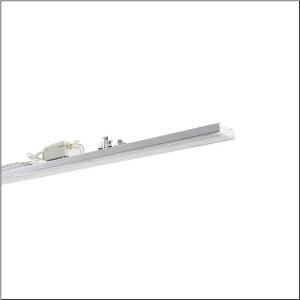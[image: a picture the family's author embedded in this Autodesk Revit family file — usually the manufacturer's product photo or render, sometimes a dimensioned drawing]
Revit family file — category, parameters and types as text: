
# Revit family: licross_r__21_recessed_ho_52tl12dn1e5m_37b9
name_source: partatom
category: Lighting Fixtures
units: mm (PartAtom-declared; Revit-internal decimal feet)

## family parameters
Cut with Voids When Loaded = No
Host = Face
Light Source = No
Part Type = Normal
Room Calculation Point = No
Round Connector Dimension = Use Diameter
Shared = No

## types (1)
- --- (1 x LED, 14510 lm, 84.6 W, 3500K)
    Apparent Load = 85 VA
    CIE Flux Codes = 69 91 98 100 100
    Color Rendering = 80
    Color Temperature = 3500K
    Default Elevation = 1800 mm
    Description = Licross® 21 Recessed HO, luminaire insert, of sheet steel, galvanised, coil coated, white, length: 1.500mm, width: 66mm, height: 67mm, LED rated luminous flux: 14.510lm, light colour: 835, control gear: DALI 2, with plug, 5-pole, with phase selection, mains connection: 220..240V, AC, 50/60Hz, rated input power: 85W, halogen-free wiring, primary optical cover: cover, of PMMA, light emission: direct distribution, primary light characteristic: symmetric, protection rating (complete): IP40, insulation class (complete): insulation class I (protective earthing), certification: CE, ENEC, VDE, UKCA, protection symbol: D if used in an environment without relevant dust loads with corresponding accessories, impact resistance: IK06, permissible ambient temperature for indoor applications: -25..+30°C, corresponds to IFS (International Featured Standards) requirements for safety and quality in the food industry, reducing of maximum allowable ambient temperature of 5°C with ceiling mounting, LABS conformity tested according to VDMA 24364:2018-05, packaging unit: 1 piece
    Height = 58 mm
    Lamp = 1 x LED
    Lamp Light Flux = 14510 lm
    Lamp Power = 84.6 W
    Lamp count = 1
    Length = 1500 mm
    Luminous efficacy = 172 lm/W
    Manufacturer = Siteco
    ModVariant = No
    Model = 52TL12DN1E5M
    Mounting Place = Ceiling
    Mounting Type = Pendant
    Number of Poles = 1
    OnlyDefault = Yes
    Power Factor = 1
    Product Name = Licross® 21 Recessed HO
    Product group = luminaire insert
    ProductGroupID = 901
    Protection Class = Protection class I
    Protection Degree = IP 40
    RLX_Detail_Level = 1
    RLX_Emergency_Light_Flux = 0 lm
    RLX_Emergency_Type = 0
    RLX_Emergency_Type_DB = No
    RlxData = <blob elided: 24701 chars, md5=b4fcf30b>
    Socket = socket
    Standby Power = 0 W
    System Light Flux = 14510 lm
    System Power = 85 W
    Type Comments = factory setting: luminous flux: 100 % | dim-lin: 254 | 484 mA
    Type Image = l_1296930.jpg
    URL = http://relux.com
    VarID = @adj_057905
    Voltage = 0 V
    Weight = 0.00 kg
    Width = 66 mm

## geometry (parser evidence)
native form markers: Blend x4, Sweep x10
no freeform markers — native parametric forms only
